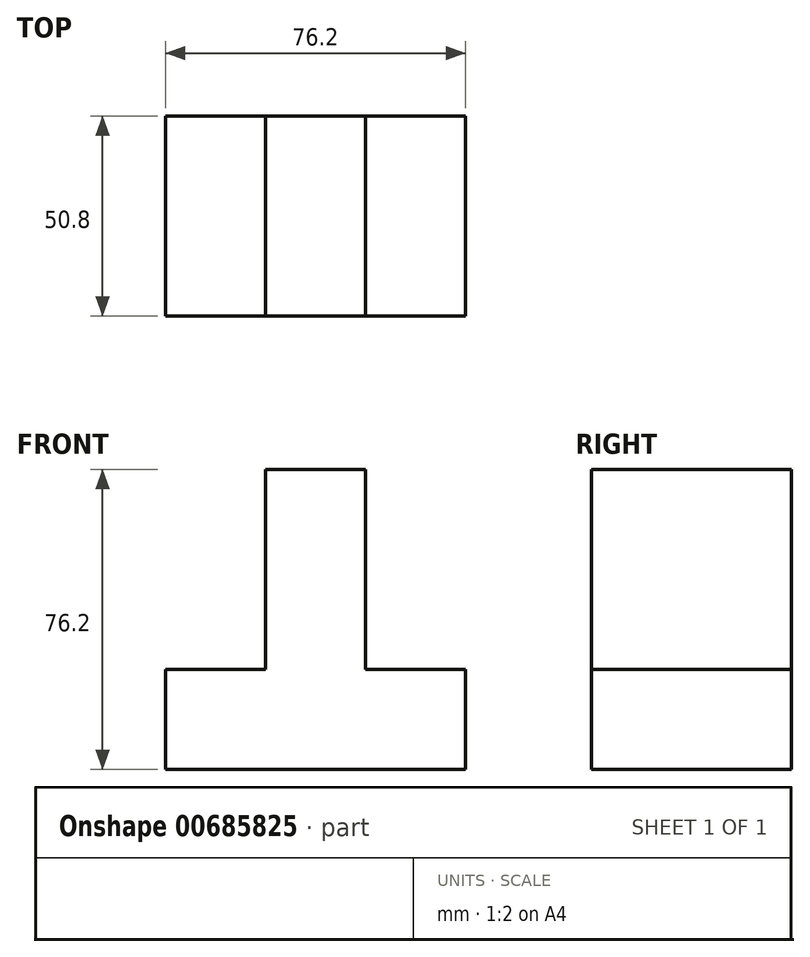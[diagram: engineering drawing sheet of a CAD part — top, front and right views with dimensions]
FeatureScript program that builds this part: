
annotation { "Feature Type Name" : "Feature", "Feature Type Description" : "" }
export const myFeature = defineFeature(function(context is Context, id is Id, definition is map)
    precondition{}
    {
        {
            var Q0;
            Q0=qCreatedBy(makeId("Front.planeOp"),FACE);
            var sketch = newSketch(context, id + "F0", { "sketchPlane" : qUnion([Q0])});
            skLineSegment(sketch, "E0", {"start": v(-50.8, -25.4) * mm, "end": v(25.4, -25.4) * mm});
            skLineSegment(sketch, "E1", {"start": v(-50.8, -25.4) * mm, "end": v(-50.8, 0) * mm});
            skLineSegment(sketch, "E2", {"start": v(-50.8, 0) * mm, "end": v(-25.4, 0) * mm});
            skLineSegment(sketch, "E3", {"start": v(-25.4, 0) * mm, "end": v(-25.4, 50.8) * mm});
            skLineSegment(sketch, "E4", {"start": v(-25.4, 50.8) * mm, "end": v(0, 50.8) * mm});
            skLineSegment(sketch, "E5", {"start": v(0, 50.8) * mm, "end": v(0, 0) * mm});
            skLineSegment(sketch, "E6", {"start": v(0, 0) * mm, "end": v(25.4, 0) * mm});
            skLineSegment(sketch, "E7", {"start": v(25.4, 0) * mm, "end": v(25.4, -25.4) * mm});
            skSolve(sketch);
        }
        {
            var Q0;
            Q0=makeQuery(id+"F0.imprint","IMPRINT",FACE,{"disambiguationData":[TD([[makeQuery(id+"F0.imprint","IMPRINT",EDGE,{"derivedFrom":sQuery(id+"F0.wireOp",EDGE,"E0")}),1.0]])]});
            extrude(context, id + "F1", {"entities" : qUnion([Q0]), "depth" : 50.8 * mm, "offsetDistance" : 25.4 * mm});
        }
    });
